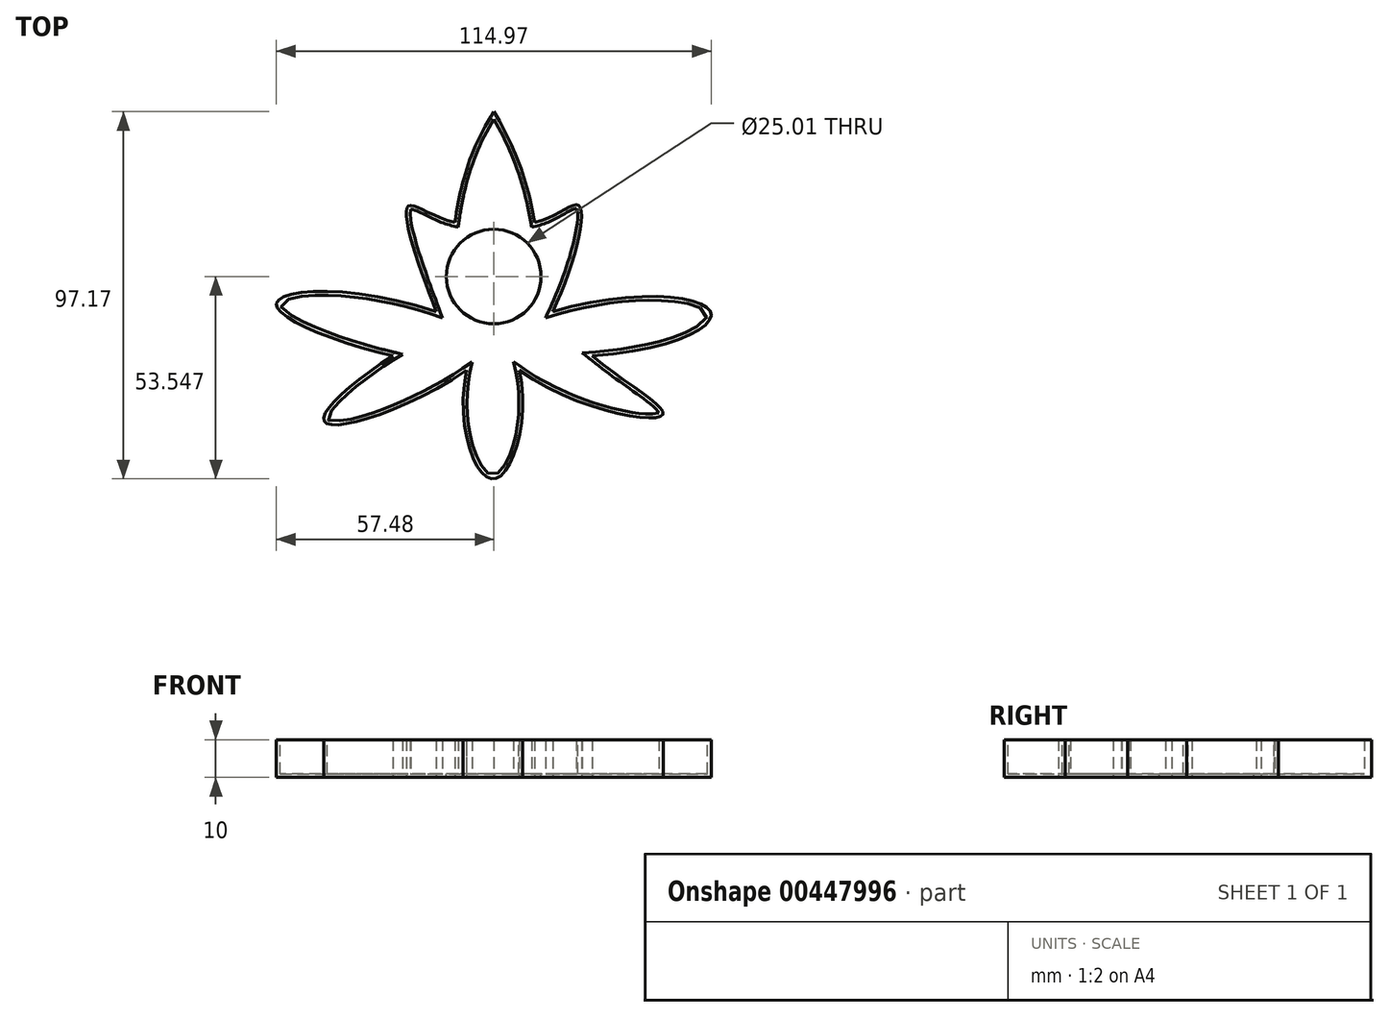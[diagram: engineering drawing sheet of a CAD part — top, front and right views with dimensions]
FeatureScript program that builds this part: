
annotation { "Feature Type Name" : "Feature", "Feature Type Description" : "" }
export const myFeature = defineFeature(function(context is Context, id is Id, definition is map)
    precondition{}
    {
        {
            var Q0;
            Q0=qCreatedBy(makeId("Top.planeOp"),FACE);
            var sketch = newSketch(context, id + "F0", { "sketchPlane" : qUnion([Q0])});
            skFitSpline(sketch, "E0", {"points": [v(0, 47.6) * mm, v(-10.27, 18.28) * mm], "startDerivative": vector(-18.88, -30.56) * mm, "endDerivative": vector(-4.47, -31.3) * mm});
            skFitSpline(sketch, "E1", {"points": [v(-10.27, 18.28) * mm, v(-22.7, 22.5) * mm, v(-15.24, -5.33) * mm], "startDerivative": vector(-47.65, 11) * mm, "endDerivative": vector(21.36, -56.54) * mm});
            skFitSpline(sketch, "E2", {"points": [v(-15.24, -5.33) * mm, v(-57.48, -3.34) * mm, v(-26.67, -17) * mm], "startDerivative": vector(-122.67, 41.82) * mm, "endDerivative": vector(96.47, -22.5) * mm});
            skFitSpline(sketch, "E3", {"points": [v(-26.67, -17) * mm, v(-44.8, -34.4) * mm, v(-7.2, -20.83) * mm], "startDerivative": vector(-73.55, -46.8) * mm, "endDerivative": vector(88.7, 59.6) * mm});
            skFitSpline(sketch, "E4", {"points": [v(-7.2, -20.83) * mm, v(0, -49.56) * mm, v(6.74, -20.83) * mm], "startDerivative": vector(-17.97, -87.13) * mm, "endDerivative": vector(-17.9, 78.98) * mm});
            skFitSpline(sketch, "E5", {"points": [v(6.74, -20.83) * mm, v(44.7, -32.58) * mm, v(26, -17) * mm], "startDerivative": vector(83.7, -58.35) * mm, "endDerivative": vector(-64.28, 52.37) * mm});
            skFitSpline(sketch, "E6", {"points": [v(26, -17) * mm, v(57.32, -5.33) * mm, v(15.57, -5.33) * mm], "startDerivative": vector(134.72, 9.6) * mm, "endDerivative": vector(-117.5, -35.4) * mm});
            skFitSpline(sketch, "E7", {"points": [v(15.57, -5.33) * mm, v(22.53, 22.75) * mm, v(10.85, 18.28) * mm], "startDerivative": vector(25.95, 54.37) * mm, "endDerivative": vector(-43, -9.35) * mm});
            skFitSpline(sketch, "E8", {"points": [v(10.85, 18.28) * mm, v(0, 47.6) * mm], "startDerivative": vector(-5.22, 30.56) * mm, "endDerivative": vector(-17.65, 29.07) * mm});
            skSolve(sketch);
        }
        {
            var Q0;
            Q0=makeQuery(id+"F0.imprint","IMPRINT",FACE,{"disambiguationData":[TD([[makeQuery(id+"F0.imprint","IMPRINT",EDGE,{"derivedFrom":sQuery(id+"F0.wireOp",EDGE,"E0")}),1.0]])]});
            extrude(context, id + "F1", {"entities" : qUnion([Q0]), "depth" : 10 * mm});
        }
        {
            var Q0;
            Q0=makeQuery(id+"F1.opExtrude","CAP_FACE",FACE,{"disambiguationData":[OSD([sQuery(id+"F0.wireOp",EDGE,"E0"),sQuery(id+"F0.wireOp",EDGE,"E1"),sQuery(id+"F0.wireOp",EDGE,"E2"),sQuery(id+"F0.wireOp",EDGE,"E3"),sQuery(id+"F0.wireOp",EDGE,"E4"),sQuery(id+"F0.wireOp",EDGE,"E5"),sQuery(id+"F0.wireOp",EDGE,"E6"),sQuery(id+"F0.wireOp",EDGE,"E7"),sQuery(id+"F0.wireOp",EDGE,"E8")])],"isStart":false});
            shell(context, id + "F2", {"entities" : qUnion([Q0]), "thickness" : 1 * mm});
        }
        {
            var Q0;
            Q0=makeQuery(id+"F2.opShell","OFFSET_FACE",FACE,{"disambiguationData":[OSD([sQuery(id+"F0.wireOp",EDGE,"E0"),sQuery(id+"F0.wireOp",EDGE,"E1"),sQuery(id+"F0.wireOp",EDGE,"E2"),sQuery(id+"F0.wireOp",EDGE,"E3"),sQuery(id+"F0.wireOp",EDGE,"E4"),sQuery(id+"F0.wireOp",EDGE,"E5"),sQuery(id+"F0.wireOp",EDGE,"E6"),sQuery(id+"F0.wireOp",EDGE,"E7"),sQuery(id+"F0.wireOp",EDGE,"E8")])]});
            var sketch = newSketch(context, id + "F3", { "sketchPlane" : qUnion([Q0])});
            skCircle(sketch, "E9", {"center": v(0, 3.98) * mm, "radius": 12.5 * mm});
            skSolve(sketch);
        }
        {
            var Q0;
            Q0=makeQuery(id+"F3.imprint","IMPRINT",FACE,{"disambiguationData":[TD([[makeQuery(id+"F3.imprint","IMPRINT",EDGE,{"derivedFrom":sQuery(id+"F3.wireOp",EDGE,"E9")}),1.0]])]});
            extrude(context, id + "F4", {"entities" : qUnion([Q0]), "operationType" : NewBodyOperationType.REMOVE, "oppositeDirection" : true, "depth" : 25 * mm});
        }
    });
